# Revit family: QL01921015
name_source: partatom
category: Apparecchi idraulici
units: mm (PartAtom-declared; Revit-internal decimal feet)

## family parameters
Basato su piano di lavoro = No
Condiviso = No
Numero OmniClass = 23.45.00.00
Punto di calcolo locali = No
Quota connettore circolare = Usa diametro
Sempre verticale = Sì
Taglio con vuoti quando caricato = No
Tipo di parte = Normale
Titolo OmniClass = Sanitary, Laundry, and Cleaning Equipment

## types (1)
- QL01921015
    Commenti sul tipo = Utilizzato per impianti idrici, applicazioni industriali ed agricole, in generale con ogni fluido non corrosivo.
Utilizzato per impianti idrici, applicazioni industriali ed agricole, in generale con ogni fluido non corrosivo.
    Descrizione = Realizzato in ottemperanza ai requisiti gestionali della norma EN ISO 9001.
Utilizzato per la regolazione della temperatura degli ambienti e comandare apparecchi degli impianti di riscaldamento e condizionamento.
    Materiale = Prodotto in lega di ottone conforme alla norma EN 12165-CW617N-DW
    Modello = Cim 40
    Pressione nominale = PN 10
    Produttore = CIMBERIO SPA
    Prospetto di default = 0 mm  [stored 0 ft]
    Temperatura di esercizio = -10÷90°C
    URL = https://web.cimberio.com

note: [stored X ft] marks values corroborated as IEEE doubles in the binary element streams (Revit-internal decimal feet)
